# Revit family: for update_453009_new
name_source: partatom
category: Plumbing Fixtures
revit_build: Autodesk Revit 2018 (Build: 20170223_1515(x64)
units: mm (PartAtom-declared; Revit-internal decimal feet)

## family parameters
Cut with Voids When Loaded = No
Host = Face
OmniClass Number = 23.31.19.00
OmniClass Title = Toilets
Part Type = Normal
Room Calculation Point = No
Round Connector Dimension = Use Diameter
Shared = No

## types (1)
- ME by Starck Toilet set wall-mounted 370x480x390 mm - 45300900A1
    Always visible = Yes
    Connector Description = Water Inlet 55 mm
    Default Elevation = 1219 mm
    Depth = 480 mm  [stored 1.5748 ft]
    Description = Duravit ME by Starck Toilet set wall-mounted 370x480x390 mm - 45300900A1
    Diameter = 55  [stored 0.180446 ft]
    Edition number = 1
    Height = 390 mm  [stored 1.27953 ft]
    IFC Classification = Sanitary Terminal
    Manufacturer = Duravit
    Manufacturer name = DURAVIT AG
    Masterformat 2014 Code = 01 52 19
    Masterformat 2014 Description = Sanitary Facilities
    Material 1 = Duravit - Ceramic - 00 - White Alpin
    Material 2 = Duravit - Metal - Chrome
    Material main = Ceramics
    Model = ME by Starck Toilet set wall-mounted 370x480x390 mm - 453009
    OmniClass Code = 23-31 19 00
    OmniClass Description = Toilets
    Outlet Connector Description = Sanitary outlet 102 mm
    Outlet Diameter = 102
    Product Guid = 337177c4-8870-47d1-9bce-f6baa94266d1
    Product SKU = ME-by-Starck-Toilet-set-wall-mounted--370x480x390-mm-453009
    Product data url = https://bimobject.com
    Product name = ME by Starck Toilet set wall-mounted  370x480x390 mm - 453009
    QR code = https://bimobject.com
    UNSPSC Code = 301815
    URL = http://pro.duravit.com
    Uniclass 2015 Code = Pr_40_20_93
    Uniclass 2015 Name = Urinal and WC fittings
    Uniformat II Code = D2030
    Uniformat II Description = Sanitary Waste
    Weight = 25.80 kg
    Width = 370 mm  [stored 1.21391 ft]

note: [stored X ft] marks values corroborated as IEEE doubles in the binary element streams (Revit-internal decimal feet)

## geometry (parser evidence)
native form markers: Sweep x4
no freeform markers — native parametric forms only
